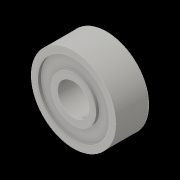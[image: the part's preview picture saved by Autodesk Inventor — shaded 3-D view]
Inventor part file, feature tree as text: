
AUTODESK INVENTOR PART (.ipt)
format: ipt  version: 2016 (Build 200138000, 138)  size: 120,832 bytes
history: native  units: in
note: dims shown in document units (in); Inventor stores cm internally (conversion verified against a paired STEP export)
features: revolve x1
ambient origin geometry x8: Origin, YZ Plane, XZ Plane, XY Plane, X Axis, Y Axis, Z Axis, Center Point
bodies: Solid1 (feature_tree)
feature tree (1):
  revolve  "Revolve1"  [1 undecoded]
note: 1 required parameter value undecoded (feature->parameter linkage not recoverable at this tier; creation-order binding heuristic only, values carry confidence <= 0.55)
